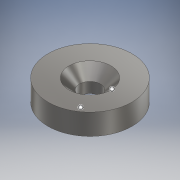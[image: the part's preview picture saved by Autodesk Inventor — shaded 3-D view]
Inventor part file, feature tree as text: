
AUTODESK INVENTOR PART (.ipt)
format: ipt  version: 2019 (Build 230136000, 136)  size: 114,688 bytes
history: native  units: mm
features: sketch x2, sheet_metal_op x1, hole x1, other x1
ambient origin geometry x8: Origin, YZ Plane, XZ Plane, XY Plane, X Axis, Y Axis, Z Axis, Center Point
bodies: Solid1 (feature_tree)
feature tree (5):
  sheet_metal_op  "Face1"
  hole  "Hole1"  [1 undecoded]
  sketch  "Sketch1"  dims[d0=20.0mm d1=0.8mm]
  other  "Plate1"
  sketch  "Sketch2"  dims[d2=5.0mm d3=5.0mm d4=5.0mm d5=10.0mm d6=2.0mm d7=90.0deg d8=5.0mm d9=20.594885mm d10=0.0mm d11=0.0mm]
note: 1 required parameter value undecoded (feature->parameter linkage not recoverable at this tier; creation-order binding heuristic only, values carry confidence <= 0.55)
